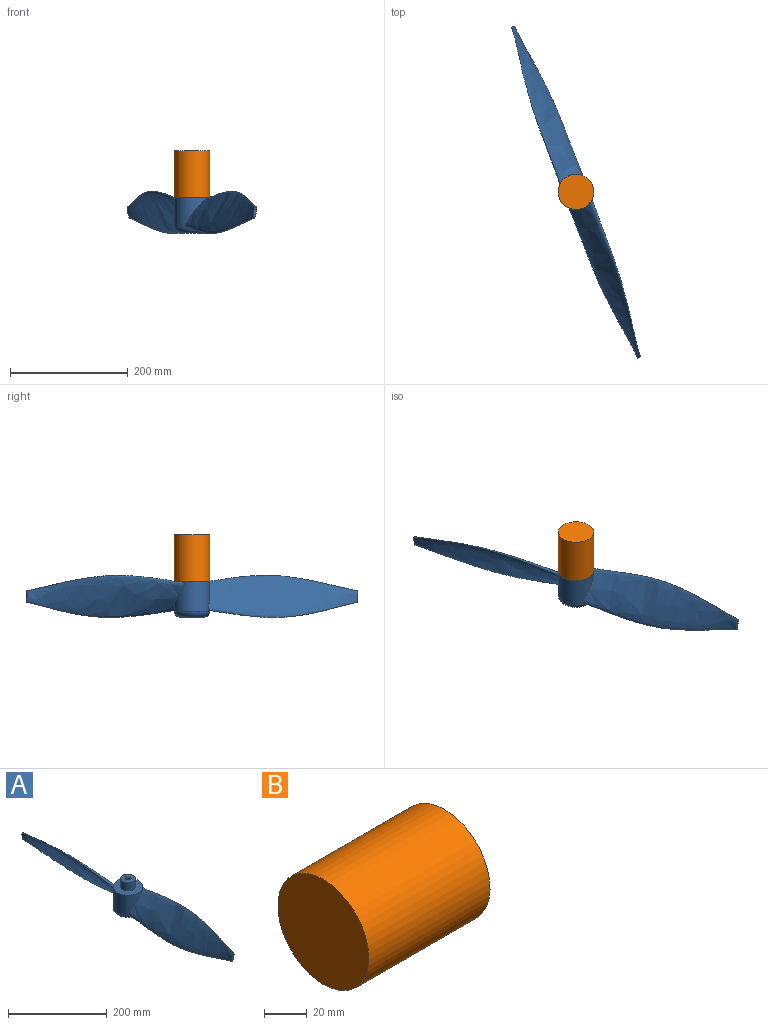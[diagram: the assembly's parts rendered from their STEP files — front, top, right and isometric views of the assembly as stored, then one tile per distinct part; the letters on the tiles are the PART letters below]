
ASSEMBLY  parts=2 mates=1
PART A: 15 faces, bbox 64.9x600x80.6 mm
  f0: plane 30x30mm, normal (0,0,1), area 624.5mm2, adj f1,f8,f9,f10,f11
  f1: cylinder r=15mm len=30mm, axis (0,0,1), area 1885mm2, adj f0,f2
  f2: plane 60x60mm, normal (0,0,1), area 2120.6mm2, adj f1,f3
  f3: cylinder r=30mm len=60mm, axis (0,0,1), area 8055mm2, adj f2,f5,f7,f13
  f4: plane 40x40mm, normal (0,0,-1), area 1256.6mm2, adj f7
  f5: bspline ~278.38x71.16mm, area 35603.5mm2, adj f3,f6
  f6: plane 19.74x6.03mm, normal (0,1,0), area 78.5mm2, adj f5
  f7: torus R=20mm, axis (0,0,1), area 2602.2mm2, adj f3,f4
  f8: plane 20x2mm, normal (0,-1,0), area 40mm2, adj f0,f9,f11,f12
  f9: plane 20x2mm, normal (1,0,0), area 40mm2, adj f0,f8,f10,f12
  f10: cylinder r=5mm len=20mm, axis (0,0,1), area 588mm2, adj f0,f9,f11,f12
  f11: plane 20x2mm, normal (-1,0,0), area 40mm2, adj f0,f8,f10,f12
  f12: plane 11.9x10mm, normal (0,0,1), area 82.4mm2, adj f8,f9,f10,f11
  f13: bspline ~278.38x71.16mm, area 35603.5mm2, adj f3,f14
  f14: plane 19.74x6.03mm, normal (0,-1,0), area 78.5mm2, adj f13
PART B: 5 faces, bbox 95x60x60 mm
  f0: plane 60x60mm, normal (-1,0,0), area 2827.4mm2, adj f4
  f1: plane 10x10mm, normal (1,0,0), area 78.5mm2, adj f2
  f2: cylinder r=5mm len=15mm, axis (-1,0,0), area 471.2mm2, adj f1,f3
  f3: plane 60x60mm, normal (1,0,0), area 2748.9mm2, adj f2,f4
  f4: cylinder r=30mm len=80mm, axis (-1,0,0), area 15079.6mm2, adj f0,f3
PLACE A rot(axis=(0,0,1),20.8deg) t=(-91.45,-101.03,58.29)mm
PLACE B rot(axis=(0.71,0,-0.71),180deg) t=(-91.45,-101.03,127.9)mm fixed
MATE revolute A.f1 <-> B.f2  axis (0,0,1) through (-91.45,-101.03,83.29)mm
